# Revit family: Gira_543500
name_source: partatom
category: Elektroinstallationen
revit_build: Autodesk Revit 2017 (Build: 20160225_1515(x64)
units: mm (PartAtom-declared; Revit-internal decimal feet)

## family parameters
Basisbauteil = Fläche
Beim Laden mit Abzugskörper schneiden = Nein
Bemaßung runder Anschluss = Durchmesser verwenden
Beschriftungsausrichtung beibehalten = Nein
Gemeinsam genutzt = Nein
Raumberechnungspunkt = Nein
Teiletyp = Normal

## types (1)
- Funk Schalt-/Tastakt. 8f/Jal.akt. 4f REG Gira eNet
    Andere Bussysteme = eNet
    Anzahl der Ausgänge = 0
    Anzahl der Eingänge = 3
    Anzahl der binären Eingänge = 0
    BIM = https://media.stage.bim.site 8f.rfa
    BIMSITE_PRODUCT_ID = 5c32498b0bdf5b55e7922cb201f5f3a17eece12c
    Beschreibung = eNet Funk Schalt- bzw. Tastaktor 8fach   Jalousieaktor 4fach  REG Merkmale: Mit eNet Server einstellbar::  Vollverschlüsselte Funkübertragung (AES-CCM) ab eNet Server Software Version 2.0.  Bediensperren.  Update der Gerätesoftware.  Der eNet Funk Schalt-bzw. Tast- oder Jalousieaktor empfängt über eine Datenleitung vom eNet Funk Empfangsmodul oder eNet Server Telegramme zum Schalten von Beleuchtungen oder zur Steuerung elektrisch betriebener Behänge.  Es werden jeweils zwei Ausgänge in der gleichen Betriebsart (Schalten, Tasten, Jalousie oder Rolllade) betrieben.  Schalten von Beleuchtung oder einphasigen Lüftermotoren.  Steuern elektrisch betriebener Behänge, wie z. B. Jalousien, Rollläden oder Markisen.  Betriebsarten: Schaltaktor, Tastaktor pro Ausgang oder Jalousieaktor, Rollladenaktor für paarweise Ausgänge einstellbar.  Statusrückmeldung an eNet Funksender.  Szenenbetrieb.  Betriebsart Tasten: Relaiskontakt bleibt so lange geschlossen wie Telegramme empfangen werden (max. 60 Sekunden).  Positionierung von Jalousie und Lamelle über Szenenaufruf.  Positionen für Sonnenschutz und Dämmerung speicherbar.  Schwellwertszenen für Sonnenschutz, Dämmerung und Windalarm.  Behanglaufzeit speicherbar.  Lamellenumsteuerzeit speicherbar. Mit eNet Server einstellbar::  Blinkfunktion.  Nachlaufzeit.  Ein- bzw. Ausschaltverzögerung.  Abschaltvorwarnung.  Minimale Schaltwiederholzeit.  Dauer-Ein, Dauer-Aus.  Umsteuerzeit bei Richtungswechsel.  Laufrichtung invertierbar (z. B. für Dachfenster).  Position bei Sonnenschutz, Dämmerung, Aussperrschutz und Windalarm.  Hinweise :  Zum Betrieb dieses Reiheneinbaugeräts wird ein eNet Funk Empfangsmodul oder ein eNet Server benötigt.
    Blindleistung = Nein
    Breite in Teilungseinheiten = 4
    Busspannung pufferbar = Nein
    Bussystem Funkbus = Ja
    Bussystem KNX = Nein
    Bussystem KNX-Funk = Nein
    Bussystem LON = Nein
    Bussystem Powernet = Nein
    Datenblatt = https://media.stage.bim.site
    Datenblatt 1 = https://media.stage.bim.site
    Funktion Schalten = Ja
    GTIN = 4010337774280
    Geeignet für C-Last = Nein
    HAN = 543500
    Handschaltung = Nein
    HeinzeBIM = https://www.heinze.de
    Hersteller = Gira
    Kosten = 0 $
    LED ansteuern = Nein
    Max. Anzahl der Jalousieausgänge = 4
    Max. Anzahl der Schaltausgänge = 0
    Max. Ausgangsstrom = 0 A
    Max. Schaltleistung [Voltampere] = 2300
    Max. Schaltstrom = 0 A
    Mit Busankopplung = Nein
    Mit LED-Anzeige = Nein
    Modulare Erweiterungsmöglichkeit = Nein
    Montageart = REG
    Produktseite = https://media.stage.bim.site
    Schaltstrom ohmsch = 16 A
    Schutzart (IP) = IP20
    Stellgröße schaltend = Nein
    Stellgröße stetig = Nein
    Stromart = AC
    Tarifumschaltung = Nein
    Typname = Funk Schalt-/Tastakt. 8f/Jal.akt. 4f REG Gira eNet
    URL = https://www.gira.de
    Ventilschutzfunktion = Nein
    Verschiedene Phasen anschließbar = Nein
    Vor Ort-/Handbedienung = Nein
    Vorgabe-Ansicht = 1219 mm
    Zulassung nach PTB = Nein

## geometry (parser evidence)
native form markers: Sweep x3
no freeform markers — native parametric forms only
